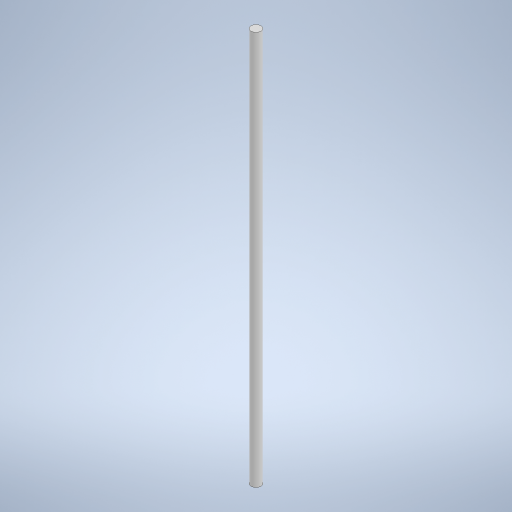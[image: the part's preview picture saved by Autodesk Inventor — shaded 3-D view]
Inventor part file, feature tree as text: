
AUTODESK INVENTOR PART (.ipt)
format: ipt  version: 2024 (Build 280153000, 153)  size: 230,912 bytes
history: native  units: mm
features: extrude x1
ambient origin geometry x8: Origin, YZ Plane, XZ Plane, XY Plane, X Axis, Y Axis, Z Axis, Center Point
bodies: Solid1 (feature_tree)
feature tree (1):
  extrude  "Extrusion1"  Depth=19.05mm
